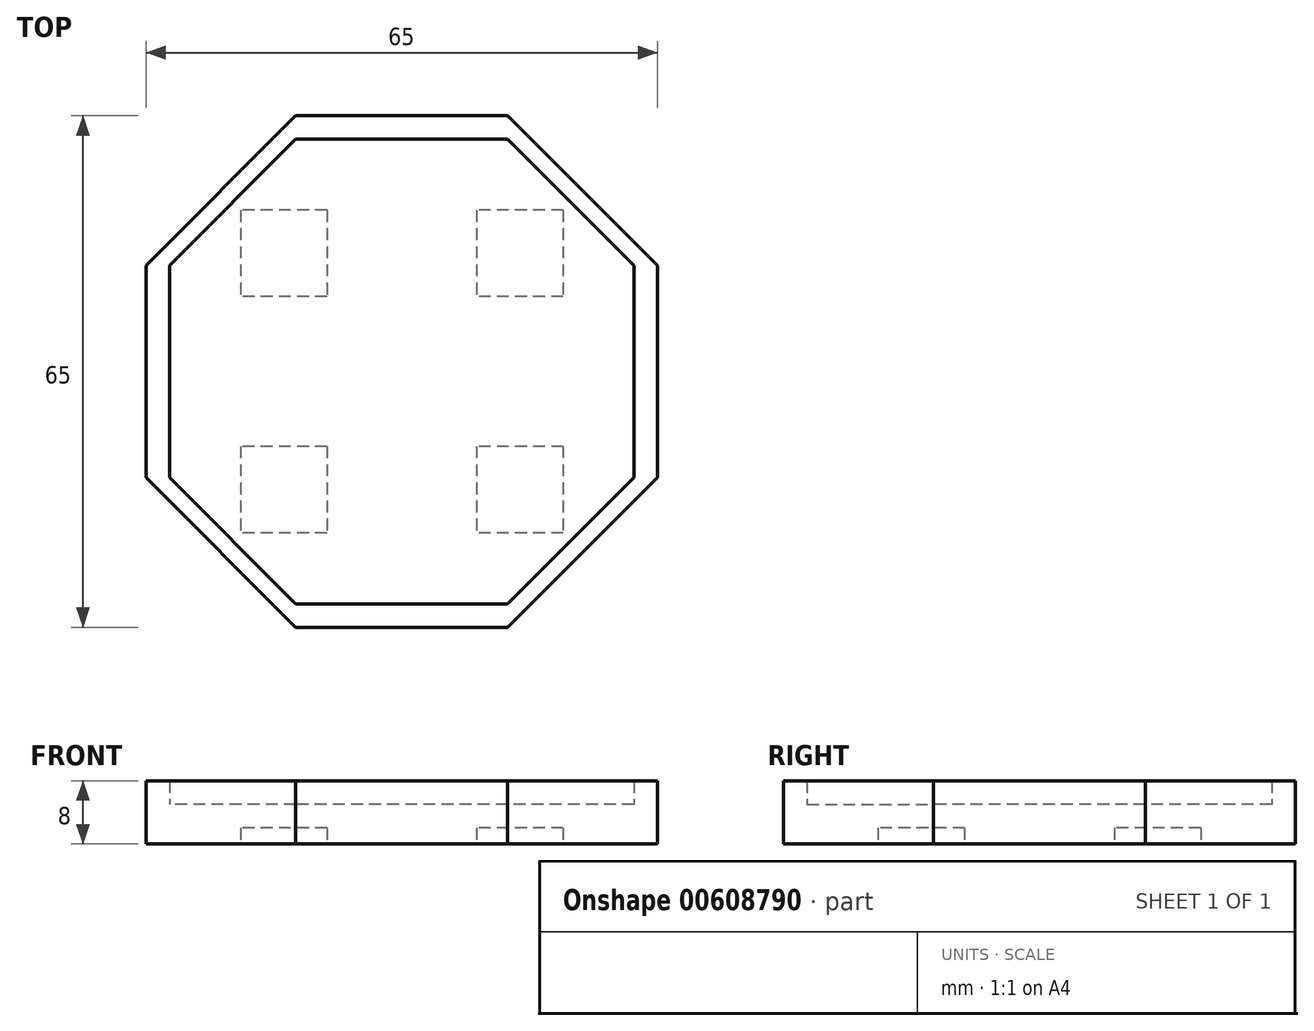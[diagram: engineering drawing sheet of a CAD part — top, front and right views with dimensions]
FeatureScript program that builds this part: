
annotation { "Feature Type Name" : "Feature", "Feature Type Description" : "" }
export const myFeature = defineFeature(function(context is Context, id is Id, definition is map)
    precondition{}
    {
        {
            var Q0;
            Q0=qCreatedBy(makeId("Top.planeOp"),FACE);
            var sketch = newSketch(context, id + "F0", { "sketchPlane" : qUnion([Q0])});
            skCircle(sketch, "E0.cCircle", {"center": v(0, 0) * mm, "radius": 32.5 * mm, "construction": true});
            skLineSegment(sketch, "E0.0", {"start": v(13.46, -32.5) * mm, "end": v(-13.46, -32.5) * mm});
            skLineSegment(sketch, "E0.1", {"start": v(-13.46, -32.5) * mm, "end": v(-32.5, -13.46) * mm});
            skLineSegment(sketch, "E0.2", {"start": v(-32.5, -13.46) * mm, "end": v(-32.5, 13.46) * mm});
            skLineSegment(sketch, "E0.3", {"start": v(-32.5, 13.46) * mm, "end": v(-13.46, 32.5) * mm});
            skLineSegment(sketch, "E0.4", {"start": v(-13.46, 32.5) * mm, "end": v(13.46, 32.5) * mm});
            skLineSegment(sketch, "E0.5", {"start": v(13.46, 32.5) * mm, "end": v(32.5, 13.46) * mm});
            skLineSegment(sketch, "E0.6", {"start": v(32.5, 13.46) * mm, "end": v(32.5, -13.46) * mm});
            skLineSegment(sketch, "E0.7", {"start": v(32.5, -13.46) * mm, "end": v(13.46, -32.5) * mm});
            skPoint(sketch, "E0.0.midPoint", {"position": v(0, -32.5) * mm});
            skSolve(sketch);
        }
        {
            var Q0;
            Q0=makeQuery(id+"F0.imprint","IMPRINT",FACE,{"disambiguationData":[TD([[makeQuery(id+"F0.imprint","IMPRINT",EDGE,{"derivedFrom":sQuery(id+"F0.wireOp",EDGE,"E0.0")}),-1.0]])]});
            extrude(context, id + "F1", {"entities" : qUnion([Q0]), "depth" : 5 * mm, "offsetDistance" : 25 * mm});
        }
        {
            var Q0;
            Q0=makeQuery(id+"F1.opExtrude","CAP_FACE",FACE,{"disambiguationData":[OSD([sQuery(id+"F0.wireOp",EDGE,"E0.0"),sQuery(id+"F0.wireOp",EDGE,"E0.1"),sQuery(id+"F0.wireOp",EDGE,"E0.2"),sQuery(id+"F0.wireOp",EDGE,"E0.3"),sQuery(id+"F0.wireOp",EDGE,"E0.4"),sQuery(id+"F0.wireOp",EDGE,"E0.5"),sQuery(id+"F0.wireOp",EDGE,"E0.6"),sQuery(id+"F0.wireOp",EDGE,"E0.7")])],"isStart":false});
            var sketch = newSketch(context, id + "F2", { "sketchPlane" : qUnion([Q0])});
            skLineSegment(sketch, "E1", {"start": v(-32.5, 13.46) * mm, "end": v(-29.5, 13.46) * mm});
            skLineSegment(sketch, "E2", {"start": v(-29.5, 13.46) * mm, "end": v(-29.5, -13.46) * mm});
            skLineSegment(sketch, "E3", {"start": v(-29.5, -13.46) * mm, "end": v(-32.5, -13.46) * mm});
            skLineSegment(sketch, "E4", {"start": v(-32.5, -13.46) * mm, "end": v(-29.5, -13.46) * mm});
            skLineSegment(sketch, "E5", {"start": v(-29.5, -13.46) * mm, "end": v(-13.46, -29.5) * mm});
            skLineSegment(sketch, "E6", {"start": v(13.46, -29.5) * mm, "end": v(-13.46, -29.5) * mm});
            skLineSegment(sketch, "E7", {"start": v(13.46, -29.5) * mm, "end": v(29.5, -13.46) * mm});
            skLineSegment(sketch, "E8", {"start": v(-13.46, -29.5) * mm, "end": v(-13.46, -32.5) * mm});
            skLineSegment(sketch, "E9", {"start": v(-13.46, -32.5) * mm, "end": v(13.46, -32.5) * mm});
            skLineSegment(sketch, "E10", {"start": v(13.46, -29.5) * mm, "end": v(13.46, -32.5) * mm});
            skLineSegment(sketch, "E11", {"start": v(13.46, -32.5) * mm, "end": v(32.5, -13.46) * mm});
            skLineSegment(sketch, "E12", {"start": v(29.5, -13.46) * mm, "end": v(32.5, -13.46) * mm});
            skLineSegment(sketch, "E13", {"start": v(-32.5, 13.46) * mm, "end": v(-13.46, 32.5) * mm});
            skLineSegment(sketch, "E14", {"start": v(13.46, 32.5) * mm, "end": v(-13.46, 32.5) * mm});
            skLineSegment(sketch, "E15", {"start": v(13.46, 32.5) * mm, "end": v(32.5, 13.46) * mm});
            skLineSegment(sketch, "E16", {"start": v(32.5, 13.46) * mm, "end": v(32.5, -13.46) * mm});
            skLineSegment(sketch, "E17", {"start": v(29.5, -13.46) * mm, "end": v(29.5, 13.46) * mm});
            skLineSegment(sketch, "E18", {"start": v(29.5, 13.46) * mm, "end": v(13.46, 29.5) * mm});
            skLineSegment(sketch, "E19", {"start": v(13.46, 29.5) * mm, "end": v(-13.46, 29.5) * mm});
            skLineSegment(sketch, "E20", {"start": v(-13.46, 29.5) * mm, "end": v(-29.5, 13.46) * mm});
            skLineSegment(sketch, "E21", {"start": v(-32.5, -13.46) * mm, "end": v(-13.46, -32.5) * mm});
            skLineSegment(sketch, "E22", {"start": v(-32.5, -13.46) * mm, "end": v(-32.5, 13.46) * mm});
            skSolve(sketch);
        }
        {
            var Q0;
            Q0 = qSketchRegion(id + "F2", true);
            extrude(context, id + "F3", {"entities" : qUnion([Q0]), "operationType" : NewBodyOperationType.ADD, "depth" : 3 * mm, "offsetDistance" : 25 * mm});
        }
        {
            var Q0;
            Q0=makeQuery(id+"F1.opExtrude","CAP_FACE",FACE,{"disambiguationData":[OSD([sQuery(id+"F0.wireOp",EDGE,"E0.0"),sQuery(id+"F0.wireOp",EDGE,"E0.1"),sQuery(id+"F0.wireOp",EDGE,"E0.2"),sQuery(id+"F0.wireOp",EDGE,"E0.3"),sQuery(id+"F0.wireOp",EDGE,"E0.4"),sQuery(id+"F0.wireOp",EDGE,"E0.5"),sQuery(id+"F0.wireOp",EDGE,"E0.6"),sQuery(id+"F0.wireOp",EDGE,"E0.7")])],"isStart":true});
            var sketch = newSketch(context, id + "F4", { "sketchPlane" : qUnion([Q0])});
            skLineSegment(sketch, "E23.bottom", {"start": v(25, -25) * mm, "end": v(-25, -25) * mm});
            skLineSegment(sketch, "E23.top", {"start": v(25, 25) * mm, "end": v(-25, 25) * mm});
            skLineSegment(sketch, "E23.left", {"start": v(25, -25) * mm, "end": v(25, 25) * mm});
            skLineSegment(sketch, "E23.right", {"start": v(-25, -25) * mm, "end": v(-25, 25) * mm});
            skPoint(sketch, "E23.middle", {"position": v(0, 0) * mm});
            skLineSegment(sketch, "E24.bottom", {"start": v(-9.5, 9.5) * mm, "end": v(-20.5, 9.5) * mm});
            skLineSegment(sketch, "E24.top", {"start": v(-9.5, 20.5) * mm, "end": v(-20.5, 20.5) * mm});
            skLineSegment(sketch, "E24.left", {"start": v(-9.5, 9.5) * mm, "end": v(-9.5, 20.5) * mm});
            skLineSegment(sketch, "E24.right", {"start": v(-20.5, 9.5) * mm, "end": v(-20.5, 20.5) * mm});
            skPoint(sketch, "E24.middle", {"position": v(-15, 15) * mm});
            skPoint(sketch, "E25.0.1.0", {"position": v(-15, -15) * mm});
            skLineSegment(sketch, "E25.0.1.1", {"start": v(-9.5, -20.5) * mm, "end": v(-20.5, -20.5) * mm});
            skLineSegment(sketch, "E25.0.1.2", {"start": v(-9.5, -9.5) * mm, "end": v(-20.5, -9.5) * mm});
            skLineSegment(sketch, "E25.0.1.3", {"start": v(-9.5, -20.5) * mm, "end": v(-9.5, -9.5) * mm});
            skLineSegment(sketch, "E25.0.1.4", {"start": v(-20.5, -20.5) * mm, "end": v(-20.5, -9.5) * mm});
            skPoint(sketch, "E25.1.0.0", {"position": v(15, 15) * mm});
            skLineSegment(sketch, "E25.1.0.1", {"start": v(20.5, 9.5) * mm, "end": v(9.5, 9.5) * mm});
            skLineSegment(sketch, "E25.1.0.2", {"start": v(20.5, 20.5) * mm, "end": v(9.5, 20.5) * mm});
            skLineSegment(sketch, "E25.1.0.3", {"start": v(20.5, 9.5) * mm, "end": v(20.5, 20.5) * mm});
            skLineSegment(sketch, "E25.1.0.4", {"start": v(9.5, 9.5) * mm, "end": v(9.5, 20.5) * mm});
            skPoint(sketch, "E25.1.1.0", {"position": v(15, -15) * mm});
            skLineSegment(sketch, "E25.1.1.1", {"start": v(20.5, -20.5) * mm, "end": v(9.5, -20.5) * mm});
            skLineSegment(sketch, "E25.1.1.2", {"start": v(20.5, -9.5) * mm, "end": v(9.5, -9.5) * mm});
            skLineSegment(sketch, "E25.1.1.3", {"start": v(20.5, -20.5) * mm, "end": v(20.5, -9.5) * mm});
            skLineSegment(sketch, "E25.1.1.4", {"start": v(9.5, -20.5) * mm, "end": v(9.5, -9.5) * mm});
            skLineSegment(sketch, "E25.direction1", {"start": v(-20.5, 9.5) * mm, "end": v(9.5, 9.5) * mm, "construction": true});
            skLineSegment(sketch, "E25.direction2", {"start": v(-20.5, 9.5) * mm, "end": v(-20.5, -20.5) * mm, "construction": true});
            skSolve(sketch);
        }
        {
            var Q0;
            Q0=makeQuery(id+"F4.imprint","IMPRINT",FACE,{"disambiguationData":[TD([[makeQuery(id+"F4.imprint","IMPRINT",EDGE,{"derivedFrom":sQuery(id+"F4.wireOp",EDGE,"E24.bottom")}),-1.0]])]});
            var Q1;
            Q1=makeQuery(id+"F4.imprint","IMPRINT",FACE,{"disambiguationData":[TD([[makeQuery(id+"F4.imprint","IMPRINT",EDGE,{"derivedFrom":sQuery(id+"F4.wireOp",EDGE,"E25.1.0.1")}),-1.0]])]});
            var Q2;
            Q2=makeQuery(id+"F4.imprint","IMPRINT",FACE,{"disambiguationData":[TD([[makeQuery(id+"F4.imprint","IMPRINT",EDGE,{"derivedFrom":sQuery(id+"F4.wireOp",EDGE,"E25.1.1.1")}),-1.0]])]});
            var Q3;
            Q3=makeQuery(id+"F4.imprint","IMPRINT",FACE,{"disambiguationData":[TD([[makeQuery(id+"F4.imprint","IMPRINT",EDGE,{"derivedFrom":sQuery(id+"F4.wireOp",EDGE,"E25.0.1.1")}),-1.0]])]});
            extrude(context, id + "F5", {"entities" : qUnion([Q0, Q1, Q2, Q3]), "operationType" : NewBodyOperationType.REMOVE, "oppositeDirection" : true, "depth" : 2 * mm, "offsetDistance" : 25 * mm});
        }
    });
